# Revit family: Casetes MTP
name_source: partatom
category: Installations électriques
units: mm (PartAtom-declared; Revit-internal decimal feet)

## family parameters
Basée sur le plan de construction = Non
Conserver l'orientation des annotations = Non
Cote de connecteur circulaire = Utiliser le diamètre
Couper avec des vides une fois chargée = Non
Partagée = Non
Point de calcul de pièce = Non
Toujours verticalement = Oui
Type d'élément = Normal

## types (8) — shared parameters
Altura = 43.7 mm  [stored 0.143373 ft]
Anchura (mm) = 110 mm  [stored 0.360892 ft]
Color = IDS_NOIR
Con carcasa = Oui
Con conexiones flexibles = Non
Con placa delantera = Non
E-catalogo enlace = https://www.legrand.fr
Temperatura de almacenamiento = -10°C à 60°C
Temperatura operativa = -10°C à 60°C
zero-valued in all types: Elévation par défaut

## per-type parameters (varying)
| type | Adecuado para número de conectores | Clase de la fibra óptica | Clasificación ETIM | Conectores LC | Conectores SC | Cruzado | EAN | Función | Número de conectores parte delantera | Número de conectores parte trasera | Número de pieza Legrand | Profundidad | Tipo de conector externo | Tipo de conector interno | Tipo de la fibra óptica | Visibilidad conectores LC | Visibilidad conectores SC | Visibilidad de los conectores |
| Casete MTP 24 LC OM4 panel HD Ultra | 24 | OM4 | EC001130 | Conectores LC : 24 fibras OM4 multimodal | Conectores SC : 12 fibras OM4 multimodal | Non | 3414970962140 | Casete slim alta densidad MTP | 2 | 24 | 032142 | 196 mm  [stored 0.643045 ft] | LC_DUPLEX | MT/MPO | Mutlimodal | Oui | Non | Oui |
| Casete MTP 12 SC OM4 panel HD Ultra | 12 | OM4 | EC001130 | Conectores LC : 12 fibras OM4 multimodal | Conectores SC : 12 fibras OM4 multimodal | Oui | 3414970962164 | Casete slim alta densidad MTP | 1 | 12 | 032143 | 196 mm  [stored 0.643045 ft] | SC_DUPLEX | MT/MPO | Mutlimodal | Non | Oui | Non |
| Casete MTP 24 LC OS2 panel HD Ultra | 24 | OS2 | EC001130 | Conectores LC : 24 fibras OS2 monomodal | Conectores SC : 12 fibras OM4 multimodal | Non | 3414970962188 | Casete slim alta densidad MTP | 2 | 24 | 032144 | 196 mm  [stored 0.643045 ft] | LC_DUPLEX | MT/MPO | unimodal | Oui | Non | Oui |
| Casete MTP 12 SC OS2 panel HD Ultra | 12 | OS2 | EC001130 | Conectores LC : 12 fibras OM4 multimodal | Conectores SC : 12 fibras OS2 monomodal | Oui | 3414970962201 | Casete slim alta densidad MTP | 1 | 12 | 032145 | 196 mm  [stored 0.643045 ft] | SC_DUPLEX | MT/MPO | unimodal | Non | Oui | Non |
| Casete MTP 12 LC OM4 panel HD Ultra | 12 | OM4 | EC002699 | Conectores LC : 12 fibras OM4 multimodal | Conectores SC : 12 fibras OM4 multimodal | Non | 3414971420236 | Casetes MTP alta densidad | 1 | 12 | 032148 | 200 mm  [stored 0.656168 ft] | LC_DUPLEX | MTP-M | Mutlimodal | Oui | Non | Non |
| Casete MTP 12 LC OS2 panel HD Ultra | 12 | OS2 | EC002699 | Conectores LC : 12 fibras OS2 monomodal | Conectores SC : 12 fibras OM4 multimodal | Non | 3414971420250 | Casetes MTP alta densidad | 1 | 12 | 032149 | 200 mm  [stored 0.656168 ft] | LC_DUPLEX | MTP-M | unimodal | Oui | Non | Non |
| Casete MTP 12 SC OM4 panel HDÉ_UNIVERSELLE_ULTRA | 12 | OM4 | EC002699 | Conectores LC : 12 fibras OM4 multimodal | Conectores SC : 12 fibras OM4 multimodal | Oui | 3414971929296 | Casetes MTP alta densidad | 1 | 12 | 032159 | 200 mm  [stored 0.656168 ft] | SC_DUPLEX | MTP-M | Mutlimodal | Non | Oui | Non |
| Casete MTP 12 SC OS2 polaridad universal | 12 | OS2 | EC002699 | Conectores LC : 12 fibras OM4 multimodal | Conectores SC : 12 fibras OS2 monomodal | Oui | 3414971929319 | Casetes MTP alta densidad | 1 | 12 | 032160 | 200 mm  [stored 0.656168 ft] | SC_DUPLEX | MTP-M | unimodal | Non | Oui | Non |

note: column(s) folded — value = type name in every type: Formulación BIM

note: [stored X ft] marks values corroborated as IEEE doubles in the binary element streams (Revit-internal decimal feet)
